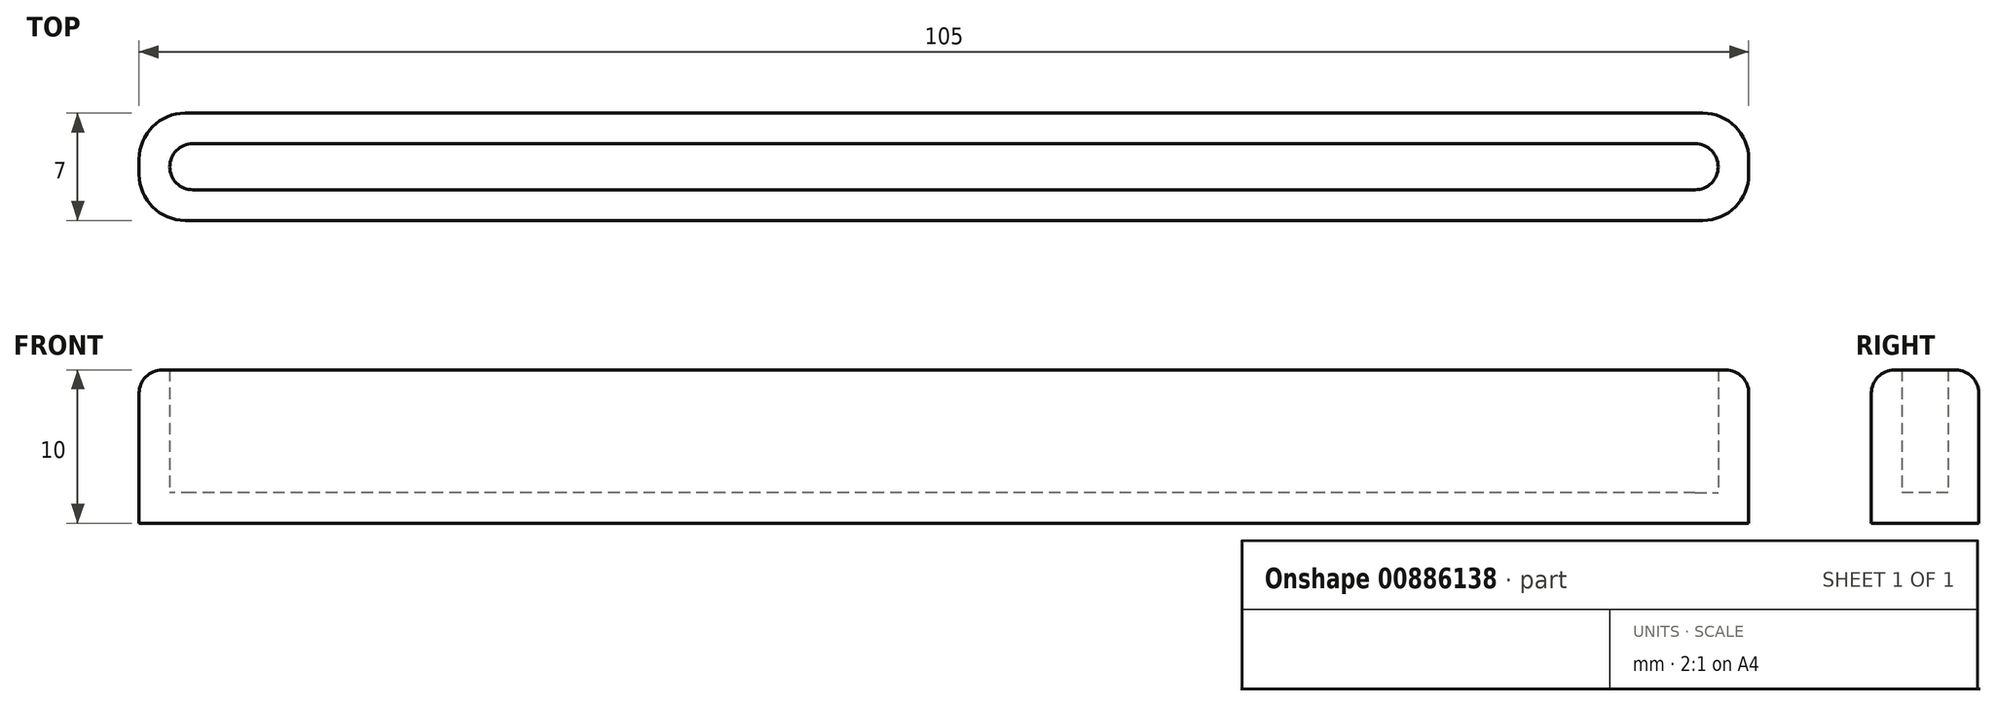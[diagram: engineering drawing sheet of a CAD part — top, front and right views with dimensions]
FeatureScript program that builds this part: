
annotation { "Feature Type Name" : "Feature", "Feature Type Description" : "" }
export const myFeature = defineFeature(function(context is Context, id is Id, definition is map)
    precondition{}
    {
        {
            var Q0;
            Q0=qCreatedBy(makeId("Top.planeOp"),FACE);
            var sketch = newSketch(context, id + "F0", { "sketchPlane" : qUnion([Q0])});
            skLineSegment(sketch, "E0.bottom", {"start": v(-52.5, 3.5) * mm, "end": v(52.5, 3.5) * mm});
            skLineSegment(sketch, "E0.top", {"start": v(-52.5, -3.5) * mm, "end": v(52.5, -3.5) * mm});
            skLineSegment(sketch, "E0.left", {"start": v(-52.5, 3.5) * mm, "end": v(-52.5, -3.5) * mm});
            skLineSegment(sketch, "E0.right", {"start": v(52.5, 3.5) * mm, "end": v(52.5, -3.5) * mm});
            skPoint(sketch, "E0.middle", {"position": v(0, 0) * mm});
            skLineSegment(sketch, "E1.bottom", {"start": v(-49, 1.5) * mm, "end": v(49, 1.5) * mm});
            skLineSegment(sketch, "E1.top", {"start": v(-49, -1.5) * mm, "end": v(49, -1.5) * mm});
            skLineSegment(sketch, "E1.left", {"start": v(-50.5, 0) * mm, "end": v(-50.5, 0) * mm});
            skLineSegment(sketch, "E1.right", {"start": v(50.5, 0) * mm, "end": v(50.5, 0) * mm});
            skPoint(sketch, "E2.visualSharp", {"position": v(-50.5, 1.5) * mm});
            skArc(sketch, "E2.filletArc", {"start": v(-49, 1.5) * mm, "mid": v(-50.06, 1.06) * mm, "end": v(-50.5, 0) * mm});
            skPoint(sketch, "E3.visualSharp", {"position": v(-50.5, -1.5) * mm});
            skArc(sketch, "E3.filletArc", {"start": v(-50.5, 0) * mm, "mid": v(-50.06, -1.06) * mm, "end": v(-49, -1.5) * mm});
            skPoint(sketch, "E4.visualSharp", {"position": v(50.5, -1.5) * mm});
            skArc(sketch, "E4.filletArc", {"start": v(49, -1.5) * mm, "mid": v(50.06, -1.06) * mm, "end": v(50.5, 0) * mm});
            skPoint(sketch, "E5.visualSharp", {"position": v(50.5, 1.5) * mm});
            skArc(sketch, "E5.filletArc", {"start": v(50.5, 0) * mm, "mid": v(50.06, 1.06) * mm, "end": v(49, 1.5) * mm});
            skSolve(sketch);
        }
        {
            var Q0;
            Q0=makeQuery(id+"F0.imprint","IMPRINT",FACE,{"disambiguationData":[TD([[makeQuery(id+"F0.imprint","IMPRINT",EDGE,{"derivedFrom":sQuery(id+"F0.wireOp",EDGE,"E1.bottom")}),-1.0]])]});
            var Q1;
            Q1=makeQuery(id+"F0.imprint","IMPRINT",FACE,{"disambiguationData":[TD([[makeQuery(id+"F0.imprint","IMPRINT",EDGE,{"derivedFrom":sQuery(id+"F0.wireOp",EDGE,"E0.bottom")}),-1.0]])]});
            extrude(context, id + "F1", {"entities" : qUnion([Q0, Q1]), "depth" : 2 * mm, "offsetDistance" : 25 * mm});
        }
        {
            var Q0;
            Q0=makeQuery(id+"F0.imprint","IMPRINT",FACE,{"disambiguationData":[TD([[makeQuery(id+"F0.imprint","IMPRINT",EDGE,{"derivedFrom":sQuery(id+"F0.wireOp",EDGE,"E0.bottom")}),-1.0]])]});
            extrude(context, id + "F2", {"entities" : qUnion([Q0]), "operationType" : NewBodyOperationType.ADD, "depth" : 10 * mm, "offsetDistance" : 25 * mm});
        }
        {
            var Q0;
            {var subQ0=sQuery(id+"F0.wireOp",EDGE,"E0.left");var subQ1=sQuery(id+"F0.wireOp",EDGE,"E0.top");Q0=makeQuery(id+"F2.boolean.opBoolean","MERGE",EDGE,{"derivedFrom":[makeQuery(id+"F1.opExtrude","SWEPT_EDGE",EDGE,{"disambiguationData":[OSD([subQ1,subQ0])]}),makeQuery(id+"F2.opExtrude","SWEPT_EDGE",EDGE,{"disambiguationData":[OSD([subQ1,subQ0])]})]});}
            var Q1;
            {var subQ0=sQuery(id+"F0.wireOp",EDGE,"E0.right");var subQ1=sQuery(id+"F0.wireOp",EDGE,"E0.top");Q1=makeQuery(id+"F2.boolean.opBoolean","MERGE",EDGE,{"derivedFrom":[makeQuery(id+"F1.opExtrude","SWEPT_EDGE",EDGE,{"disambiguationData":[OSD([subQ1,subQ0])]}),makeQuery(id+"F2.opExtrude","SWEPT_EDGE",EDGE,{"disambiguationData":[OSD([subQ1,subQ0])]})]});}
            var Q2;
            {var subQ0=sQuery(id+"F0.wireOp",EDGE,"E0.right");var subQ1=sQuery(id+"F0.wireOp",EDGE,"E0.bottom");Q2=makeQuery(id+"F2.boolean.opBoolean","MERGE",EDGE,{"derivedFrom":[makeQuery(id+"F1.opExtrude","SWEPT_EDGE",EDGE,{"disambiguationData":[OSD([subQ1,subQ0])]}),makeQuery(id+"F2.opExtrude","SWEPT_EDGE",EDGE,{"disambiguationData":[OSD([subQ1,subQ0])]})]});}
            var Q3;
            {var subQ0=sQuery(id+"F0.wireOp",EDGE,"E0.left");var subQ1=sQuery(id+"F0.wireOp",EDGE,"E0.bottom");Q3=makeQuery(id+"F2.boolean.opBoolean","MERGE",EDGE,{"derivedFrom":[makeQuery(id+"F1.opExtrude","SWEPT_EDGE",EDGE,{"disambiguationData":[OSD([subQ1,subQ0])]}),makeQuery(id+"F2.opExtrude","SWEPT_EDGE",EDGE,{"disambiguationData":[OSD([subQ1,subQ0])]})]});}
            fillet(context, id + "F3", {"entities" : qUnion([Q0, Q1, Q2, Q3]), "radius" : 3 * mm, "tangentPropagation" : true, "allowEdgeOverflow" : false});
        }
        {
            var Q0;
            Q0=makeQuery(id+"F2.opExtrude","CAP_EDGE",EDGE,{"disambiguationData":[OSD([sQuery(id+"F0.wireOp",EDGE,"E0.bottom")])],"isStart":false});
            fillet(context, id + "F4", {"entities" : qUnion([Q0]), "radius" : 1.5 * mm, "tangentPropagation" : true, "allowEdgeOverflow" : false});
        }
    });
